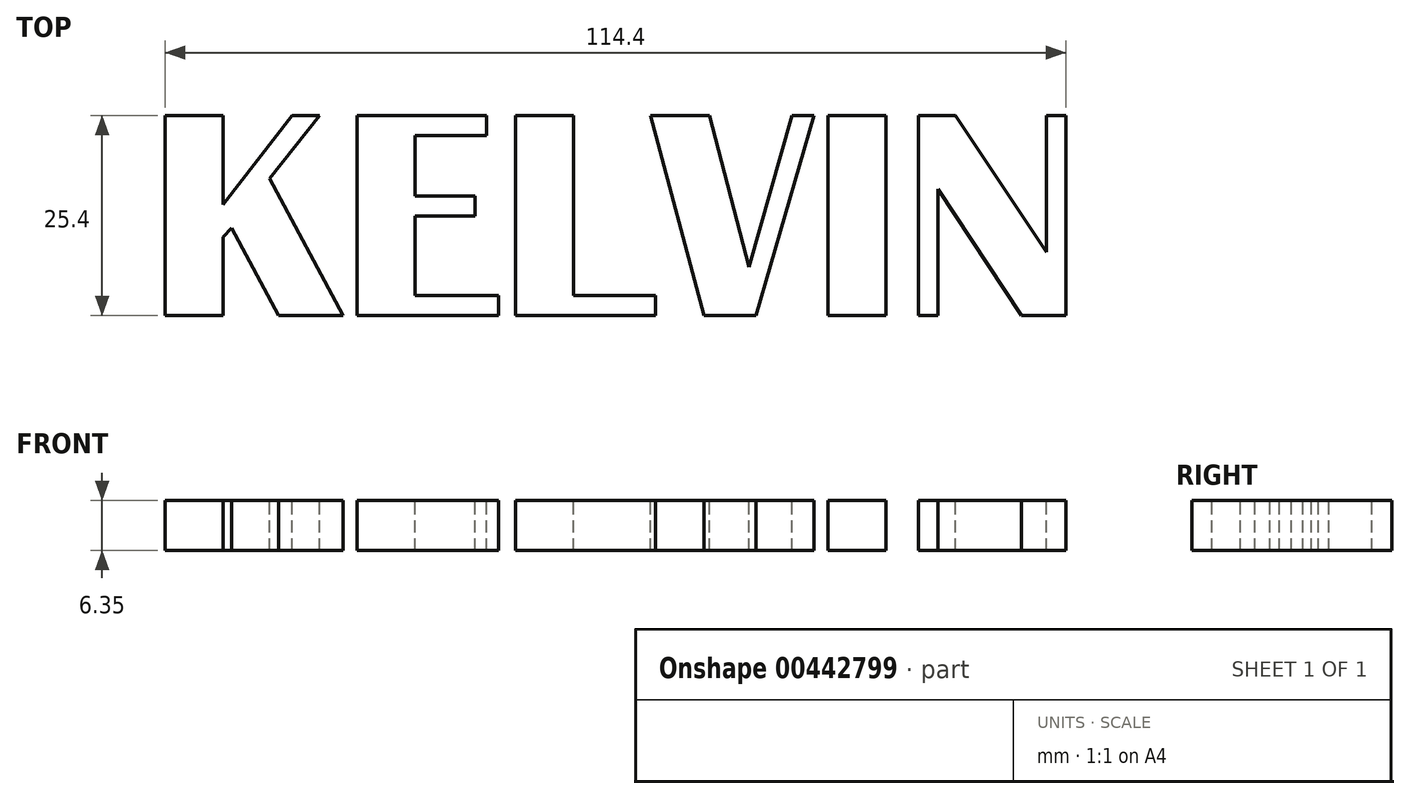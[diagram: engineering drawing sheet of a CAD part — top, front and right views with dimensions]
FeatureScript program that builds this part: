
annotation { "Feature Type Name" : "Feature", "Feature Type Description" : "" }
export const myFeature = defineFeature(function(context is Context, id is Id, definition is map)
    precondition{}
    {
        {
            var Q0;
            Q0=qCreatedBy(makeId("Top.planeOp"),FACE);
            var sketch = newSketch(context, id + "F0", { "sketchPlane" : qUnion([Q0])});
            skLineSegment(sketch, "E0", {"start": v(-142.98, 47.86) * mm, "end": v(-135.6, 47.86) * mm});
            skLineSegment(sketch, "E1", {"start": v(-135.6, 47.86) * mm, "end": v(-135.6, 36.55) * mm});
            skLineSegment(sketch, "E2", {"start": v(-135.6, 36.55) * mm, "end": v(-126.86, 47.86) * mm});
            skLineSegment(sketch, "E3", {"start": v(-126.86, 47.86) * mm, "end": v(-123.4, 47.86) * mm});
            skLineSegment(sketch, "E4", {"start": v(-123.4, 47.86) * mm, "end": v(-129.74, 39.84) * mm});
            skLineSegment(sketch, "E5", {"start": v(-129.74, 39.84) * mm, "end": v(-120.39, 22.46) * mm});
            skLineSegment(sketch, "E6", {"start": v(-120.39, 22.46) * mm, "end": v(-128.6, 22.46) * mm});
            skLineSegment(sketch, "E7", {"start": v(-128.6, 22.46) * mm, "end": v(-134.54, 33.6) * mm});
            skLineSegment(sketch, "E8", {"start": v(-134.54, 33.6) * mm, "end": v(-135.6, 32.4) * mm});
            skLineSegment(sketch, "E9", {"start": v(-135.6, 32.4) * mm, "end": v(-135.6, 22.46) * mm});
            skLineSegment(sketch, "E10", {"start": v(-135.6, 22.46) * mm, "end": v(-142.98, 22.46) * mm});
            skLineSegment(sketch, "E11", {"start": v(-142.98, 22.46) * mm, "end": v(-142.98, 47.86) * mm});
            skLineSegment(sketch, "E12", {"start": v(-118.63, 47.86) * mm, "end": v(-102.16, 47.86) * mm});
            skLineSegment(sketch, "E13", {"start": v(-102.16, 47.86) * mm, "end": v(-102.16, 45.32) * mm});
            skLineSegment(sketch, "E14", {"start": v(-102.16, 45.32) * mm, "end": v(-111.26, 45.32) * mm});
            skLineSegment(sketch, "E15", {"start": v(-111.26, 45.32) * mm, "end": v(-111.26, 37.63) * mm});
            skLineSegment(sketch, "E16", {"start": v(-111.26, 37.63) * mm, "end": v(-103.61, 37.63) * mm});
            skLineSegment(sketch, "E17", {"start": v(-103.61, 37.63) * mm, "end": v(-103.61, 35.08) * mm});
            skLineSegment(sketch, "E18", {"start": v(-103.61, 35.08) * mm, "end": v(-111.26, 35.08) * mm});
            skLineSegment(sketch, "E19", {"start": v(-111.26, 35.08) * mm, "end": v(-111.26, 25.01) * mm});
            skLineSegment(sketch, "E20", {"start": v(-111.26, 25.01) * mm, "end": v(-100.62, 25.01) * mm});
            skLineSegment(sketch, "E21", {"start": v(-100.62, 25.01) * mm, "end": v(-100.62, 22.46) * mm});
            skLineSegment(sketch, "E22", {"start": v(-100.62, 22.46) * mm, "end": v(-118.63, 22.46) * mm});
            skLineSegment(sketch, "E23", {"start": v(-118.63, 22.46) * mm, "end": v(-118.63, 47.86) * mm});
            skLineSegment(sketch, "E24", {"start": v(-98.5, 47.86) * mm, "end": v(-91.12, 47.86) * mm});
            skLineSegment(sketch, "E25", {"start": v(-91.12, 47.86) * mm, "end": v(-91.12, 25.01) * mm});
            skLineSegment(sketch, "E26", {"start": v(-91.12, 25.01) * mm, "end": v(-80.69, 25.01) * mm});
            skLineSegment(sketch, "E27", {"start": v(-80.69, 25.01) * mm, "end": v(-80.69, 22.46) * mm});
            skLineSegment(sketch, "E28", {"start": v(-80.69, 22.46) * mm, "end": v(-98.5, 22.46) * mm});
            skLineSegment(sketch, "E29", {"start": v(-98.5, 22.46) * mm, "end": v(-98.5, 47.86) * mm});
            skLineSegment(sketch, "E30", {"start": v(-81.31, 47.86) * mm, "end": v(-73.87, 47.86) * mm});
            skLineSegment(sketch, "E31", {"start": v(-73.87, 47.86) * mm, "end": v(-68.84, 28.62) * mm});
            skLineSegment(sketch, "E32", {"start": v(-68.84, 28.62) * mm, "end": v(-63.35, 47.86) * mm});
            skLineSegment(sketch, "E33", {"start": v(-63.35, 47.86) * mm, "end": v(-60.6, 47.86) * mm});
            skLineSegment(sketch, "E34", {"start": v(-60.6, 47.86) * mm, "end": v(-67.96, 22.46) * mm});
            skLineSegment(sketch, "E35", {"start": v(-67.96, 22.46) * mm, "end": v(-74.57, 22.46) * mm});
            skLineSegment(sketch, "E36", {"start": v(-74.57, 22.46) * mm, "end": v(-81.31, 47.86) * mm});
            skLineSegment(sketch, "E37", {"start": v(-58.77, 47.86) * mm, "end": v(-51.4, 47.86) * mm});
            skLineSegment(sketch, "E38", {"start": v(-51.4, 47.86) * mm, "end": v(-51.4, 22.46) * mm});
            skLineSegment(sketch, "E39", {"start": v(-51.4, 22.46) * mm, "end": v(-58.77, 22.46) * mm});
            skLineSegment(sketch, "E40", {"start": v(-58.77, 22.46) * mm, "end": v(-58.77, 47.86) * mm});
            skLineSegment(sketch, "E41", {"start": v(-47.3, 47.86) * mm, "end": v(-42.63, 47.86) * mm});
            skLineSegment(sketch, "E42", {"start": v(-42.63, 47.86) * mm, "end": v(-31.05, 30.5) * mm});
            skLineSegment(sketch, "E43", {"start": v(-31.05, 30.5) * mm, "end": v(-31.05, 47.86) * mm});
            skLineSegment(sketch, "E44", {"start": v(-31.05, 47.86) * mm, "end": v(-28.58, 47.86) * mm});
            skLineSegment(sketch, "E45", {"start": v(-28.58, 47.86) * mm, "end": v(-28.58, 22.46) * mm});
            skLineSegment(sketch, "E46", {"start": v(-28.58, 22.46) * mm, "end": v(-34.21, 22.46) * mm});
            skLineSegment(sketch, "E47", {"start": v(-34.21, 22.46) * mm, "end": v(-44.82, 38.54) * mm});
            skLineSegment(sketch, "E48", {"start": v(-44.82, 38.54) * mm, "end": v(-44.82, 22.46) * mm});
            skLineSegment(sketch, "E49", {"start": v(-44.82, 22.46) * mm, "end": v(-47.3, 22.46) * mm});
            skLineSegment(sketch, "E50", {"start": v(-47.3, 22.46) * mm, "end": v(-47.3, 47.86) * mm});
            skSolve(sketch);
        }
        {
            var Q0;
            Q0=makeQuery(id+"F0.imprint","IMPRINT",FACE,{"disambiguationData":[TD([[makeQuery(id+"F0.imprint","IMPRINT",EDGE,{"derivedFrom":sQuery(id+"F0.wireOp",EDGE,"E0")}),-1.0]])]});
            var Q1;
            Q1=makeQuery(id+"F0.imprint","IMPRINT",FACE,{"disambiguationData":[TD([[makeQuery(id+"F0.imprint","IMPRINT",EDGE,{"derivedFrom":sQuery(id+"F0.wireOp",EDGE,"E12")}),-1.0]])]});
            var Q2;
            Q2=makeQuery(id+"F0.imprint","IMPRINT",FACE,{"disambiguationData":[TD([[makeQuery(id+"F0.imprint","IMPRINT",EDGE,{"derivedFrom":sQuery(id+"F0.wireOp",EDGE,"E24")}),-1.0]])]});
            var Q3;
            Q3=makeQuery(id+"F0.imprint","IMPRINT",FACE,{"disambiguationData":[TD([[makeQuery(id+"F0.imprint","IMPRINT",EDGE,{"derivedFrom":sQuery(id+"F0.wireOp",EDGE,"E37")}),-1.0]])]});
            var Q4;
            Q4=makeQuery(id+"F0.imprint","IMPRINT",FACE,{"disambiguationData":[TD([[makeQuery(id+"F0.imprint","IMPRINT",EDGE,{"derivedFrom":sQuery(id+"F0.wireOp",EDGE,"E41")}),-1.0]])]});
            var Q5;
            Q5=makeQuery(id+"F0.imprint","IMPRINT",FACE,{"disambiguationData":[TD([[makeQuery(id+"F0.imprint","IMPRINT",EDGE,{"derivedFrom":sQuery(id+"F0.wireOp",EDGE,"E30")}),-1.0]])]});
            var Q6;
            Q6=sQuery(id+"F0.wireOp",EDGE,"E11");
            var Q7;
            Q7=sQuery(id+"F0.wireOp",EDGE,"E36");
            var Q8;
            Q8=sQuery(id+"F0.wireOp",EDGE,"E32");
            var Q9;
            Q9=sQuery(id+"F0.wireOp",EDGE,"E25");
            var Q10;
            Q10=sQuery(id+"F0.wireOp",EDGE,"E5");
            var Q11;
            Q11=sQuery(id+"F0.wireOp",EDGE,"E42");
            var Q12;
            Q12=sQuery(id+"F0.wireOp",EDGE,"E34");
            var Q13;
            Q13=sQuery(id+"F0.wireOp",EDGE,"E31");
            var Q14;
            Q14=sQuery(id+"F0.wireOp",EDGE,"E48");
            var Q15;
            Q15=sQuery(id+"F0.wireOp",EDGE,"E50");
            var Q16;
            Q16=sQuery(id+"F0.wireOp",EDGE,"E43");
            var Q17;
            Q17=sQuery(id+"F0.wireOp",EDGE,"E40");
            var Q18;
            Q18=sQuery(id+"F0.wireOp",EDGE,"E23");
            var Q19;
            Q19=sQuery(id+"F0.wireOp",EDGE,"E47");
            var Q20;
            Q20=sQuery(id+"F0.wireOp",EDGE,"E45");
            var Q21;
            Q21=sQuery(id+"F0.wireOp",EDGE,"E38");
            var Q22;
            Q22=sQuery(id+"F0.wireOp",EDGE,"E30");
            var Q23;
            Q23=sQuery(id+"F0.wireOp",EDGE,"E22");
            var Q24;
            Q24=sQuery(id+"F0.wireOp",EDGE,"E39");
            var Q25;
            Q25=sQuery(id+"F0.wireOp",EDGE,"E2");
            var Q26;
            Q26=sQuery(id+"F0.wireOp",EDGE,"E20");
            var Q27;
            Q27=sQuery(id+"F0.wireOp",EDGE,"E26");
            var Q28;
            Q28=sQuery(id+"F0.wireOp",EDGE,"E3");
            var Q29;
            Q29=sQuery(id+"F0.wireOp",EDGE,"E44");
            var Q30;
            Q30=sQuery(id+"F0.wireOp",EDGE,"E0");
            var Q31;
            Q31=sQuery(id+"F0.wireOp",EDGE,"E28");
            var Q32;
            Q32=sQuery(id+"F0.wireOp",EDGE,"E24");
            var Q33;
            Q33=sQuery(id+"F0.wireOp",EDGE,"E19");
            var Q34;
            Q34=sQuery(id+"F0.wireOp",EDGE,"E6");
            var Q35;
            Q35=sQuery(id+"F0.wireOp",EDGE,"E12");
            var Q36;
            Q36=sQuery(id+"F0.wireOp",EDGE,"E1");
            var Q37;
            Q37=sQuery(id+"F0.wireOp",EDGE,"E4");
            var Q38;
            Q38=sQuery(id+"F0.wireOp",EDGE,"E7");
            var Q39;
            Q39=sQuery(id+"F0.wireOp",EDGE,"E15");
            var Q40;
            Q40=sQuery(id+"F0.wireOp",EDGE,"E9");
            var Q41;
            Q41=sQuery(id+"F0.wireOp",EDGE,"E46");
            var Q42;
            Q42=sQuery(id+"F0.wireOp",EDGE,"E27");
            var Q43;
            Q43=sQuery(id+"F0.wireOp",EDGE,"E18");
            var Q44;
            Q44=sQuery(id+"F0.wireOp",EDGE,"E17");
            var Q45;
            Q45=sQuery(id+"F0.wireOp",EDGE,"E14");
            var Q46;
            Q46=sQuery(id+"F0.wireOp",EDGE,"E29");
            var Q47;
            Q47=sQuery(id+"F0.wireOp",EDGE,"E16");
            var Q48;
            Q48=sQuery(id+"F0.wireOp",EDGE,"E10");
            var Q49;
            Q49=sQuery(id+"F0.wireOp",EDGE,"E13");
            var Q50;
            Q50=sQuery(id+"F0.wireOp",EDGE,"E35");
            var Q51;
            Q51=sQuery(id+"F0.wireOp",EDGE,"E49");
            var Q52;
            Q52=sQuery(id+"F0.wireOp",EDGE,"E33");
            var Q53;
            Q53=sQuery(id+"F0.wireOp",EDGE,"E21");
            var Q54;
            Q54=sQuery(id+"F0.wireOp",EDGE,"E41");
            var Q55;
            Q55=sQuery(id+"F0.wireOp",EDGE,"E8");
            var Q56;
            Q56=sQuery(id+"F0.wireOp",EDGE,"E37");
            extrude(context, id + "F1", {"entities" : qUnion([Q0, Q1, Q2, Q3, Q4, Q5]), "surfaceEntities" : qUnion([Q6, Q7, Q8, Q9, Q10, Q11, Q12, Q13, Q14, Q15, Q16, Q17, Q18, Q19, Q20, Q21, Q22, Q23, Q24, Q25, Q26, Q27, Q28, Q29, Q30, Q31, Q32, Q33, Q34, Q35, Q36, Q37, Q38, Q39, Q40, Q41, Q42, Q43, Q44, Q45, Q46, Q47, Q48, Q49, Q50, Q51, Q52, Q53, Q54, Q55, Q56]), "oppositeDirection" : true, "depth" : 6.35 * mm});
        }
    });
